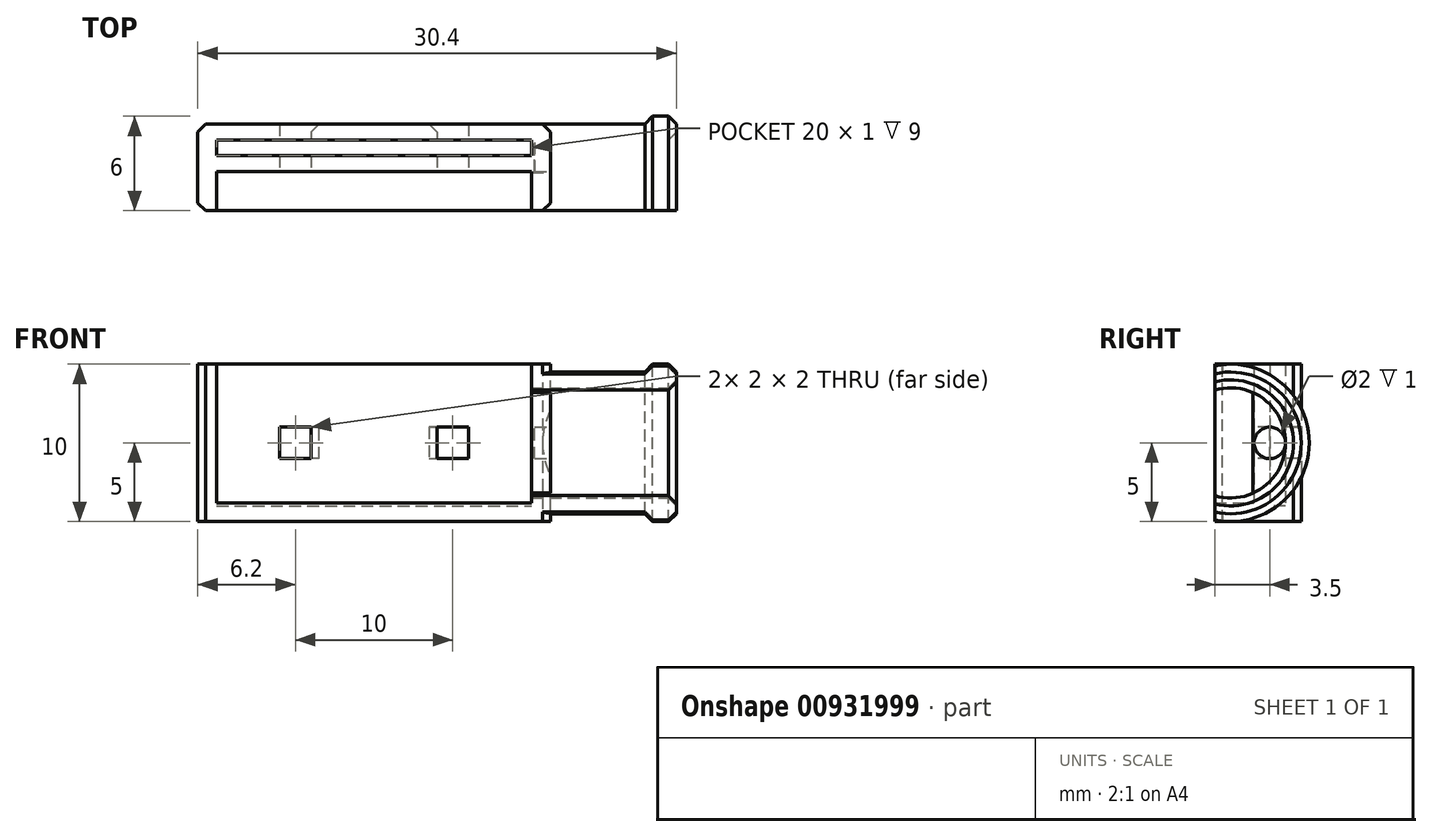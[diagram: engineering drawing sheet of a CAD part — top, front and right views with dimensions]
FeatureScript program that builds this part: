
annotation { "Feature Type Name" : "Feature", "Feature Type Description" : "" }
export const myFeature = defineFeature(function(context is Context, id is Id, definition is map)
    precondition{}
    {
        {
            var Q0;
            Q0=qCreatedBy(makeId("Top.planeOp"),FACE);
            var sketch = newSketch(context, id + "F0", { "sketchPlane" : qUnion([Q0])});
            skLineSegment(sketch, "E0.bottom", {"start": v(0, 5.5) * mm, "end": v(22.4, 5.5) * mm});
            skLineSegment(sketch, "E0.top", {"start": v(0, 0) * mm, "end": v(22.4, 0) * mm});
            skLineSegment(sketch, "E0.left", {"start": v(0, 5.5) * mm, "end": v(0, 0) * mm});
            skLineSegment(sketch, "E0.right", {"start": v(22.4, 5.5) * mm, "end": v(22.4, 0) * mm});
            skLineSegment(sketch, "E1.bottom", {"start": v(1.2, 4.5) * mm, "end": v(21.2, 4.5) * mm});
            skLineSegment(sketch, "E1.top", {"start": v(1.2, 3.5) * mm, "end": v(21.2, 3.5) * mm});
            skLineSegment(sketch, "E1.left", {"start": v(1.2, 4.5) * mm, "end": v(1.2, 3.5) * mm});
            skLineSegment(sketch, "E1.right", {"start": v(21.2, 4.5) * mm, "end": v(21.2, 3.5) * mm});
            skLineSegment(sketch, "E2.bottom", {"start": v(1.2, 0) * mm, "end": v(21.2, 0) * mm});
            skLineSegment(sketch, "E2.top", {"start": v(1.2, 2.5) * mm, "end": v(21.2, 2.5) * mm});
            skLineSegment(sketch, "E2.left", {"start": v(1.2, 0) * mm, "end": v(1.2, 2.5) * mm});
            skLineSegment(sketch, "E2.right", {"start": v(21.2, 0) * mm, "end": v(21.2, 2.5) * mm});
            skSolve(sketch);
        }
        {
            var Q0;
            Q0=makeQuery(id+"F0.imprint","IMPRINT",FACE,{"disambiguationData":[TD([[makeQuery(id+"F0.imprint","IMPRINT",EDGE,{"derivedFrom":sQuery(id+"F0.wireOp",EDGE,"E0.bottom")}),-1.0]])]});
            extrude(context, id + "F1", {"entities" : qUnion([Q0]), "depth" : 9 * mm, "offsetDistance" : 25 * mm});
        }
        {
            var Q0;
            Q0=makeQuery(id+"F1.opExtrude","CAP_FACE",FACE,{"disambiguationData":[OSD([sQuery(id+"F0.wireOp",EDGE,"E0.bottom"),sQuery(id+"F0.wireOp",EDGE,"E0.top"),sQuery(id+"F0.wireOp",EDGE,"E0.left"),sQuery(id+"F0.wireOp",EDGE,"E0.right"),sQuery(id+"F0.wireOp",EDGE,"E1.bottom"),sQuery(id+"F0.wireOp",EDGE,"E1.top"),sQuery(id+"F0.wireOp",EDGE,"E1.left"),sQuery(id+"F0.wireOp",EDGE,"E1.right")])],"isStart":true});
            var Q1;
            Q1=makeQuery(id+"F0.imprint","IMPRINT",FACE,{"disambiguationData":[TD([[makeQuery(id+"F0.imprint","IMPRINT",EDGE,{"derivedFrom":sQuery(id+"F0.wireOp",EDGE,"E1.bottom")}),-1.0]])]});
            extrude(context, id + "F2", {"entities" : qUnion([Q0, Q1]), "operationType" : NewBodyOperationType.ADD, "depth" : 1 * mm, "offsetDistance" : 25 * mm});
        }
        {
            var Q0;
            {var subQ0=sQuery(id+"F0.wireOp",EDGE,"E0.right");Q0=makeQuery(id+"F2.boolean.opBoolean","MERGE",FACE,{"derivedFrom":[makeQuery(id+"F1.opExtrude","SWEPT_FACE",FACE,{"disambiguationData":[OSD([subQ0])]}),makeQuery(id+"F2.opExtrude","SWEPT_FACE",FACE,{"disambiguationData":[OSD([subQ0])]})]});}
            var sketch = newSketch(context, id + "F3", { "sketchPlane" : qUnion([Q0])});
            skCircle(sketch, "E3", {"center": v(1, 4) * mm, "radius": 3.5 * mm});
            skCircle(sketch, "E4", {"center": v(1, 4) * mm, "radius": 4.5 * mm});
            skLineSegment(sketch, "E5", {"start": v(2.43, 7.2) * mm, "end": v(2.43, 0.8) * mm});
            skCircle(sketch, "E6", {"center": v(3.5, 4) * mm, "radius": 1 * mm});
            skSolve(sketch);
        }
        {
            var Q0;
            {var subQ0=sQuery(id+"F3.wireOp",EDGE,"E5");Q0=makeQuery(id+"F3.imprint","IMPRINT",FACE,{"disambiguationData":[TD([[makeQuery(id+"F3.imprint","IMPRINT",EDGE,{"derivedFrom":subQ0}),-1.0]])]});}
            var Q1;
            {var subQ0=sQuery(id+"F0.wireOp",EDGE,"E2.right");Q1=makeQuery(id+"F2.boolean.opBoolean","MERGE",FACE,{"derivedFrom":[makeQuery(id+"F1.opExtrude","SWEPT_FACE",FACE,{"disambiguationData":[OSD([subQ0])]}),makeQuery(id+"F2.opExtrude","SWEPT_FACE",FACE,{"disambiguationData":[OSD([subQ0])]})]});}
            extrude(context, id + "F4", {"entities" : qUnion([Q0]), "operationType" : NewBodyOperationType.REMOVE, "endBound" : BoundingType.UP_TO_SURFACE, "oppositeDirection" : true, "depth" : 25 * mm, "endBoundEntityFace" : qUnion([Q1]), "offsetDistance" : 25 * mm});
        }
        {
            var Q0;
            Q0=makeQuery(id+"F3.imprint","IMPRINT",FACE,{"disambiguationData":[TD([[makeQuery(id+"F3.imprint","IMPRINT",EDGE,{"derivedFrom":sQuery(id+"F3.wireOp",EDGE,"E6")}),1.0]])]});
            var Q1;
            {var subQ0=sQuery(id+"F0.wireOp",EDGE,"E2.right");Q1=makeQuery(id+"F2.boolean.opBoolean","MERGE",FACE,{"derivedFrom":[makeQuery(id+"F1.opExtrude","SWEPT_FACE",FACE,{"disambiguationData":[OSD([subQ0])]}),makeQuery(id+"F2.opExtrude","SWEPT_FACE",FACE,{"disambiguationData":[OSD([subQ0])]})]});}
            extrude(context, id + "F5", {"entities" : qUnion([Q0]), "operationType" : NewBodyOperationType.REMOVE, "oppositeDirection" : true, "depth" : 1 * mm, "endBoundEntityFace" : qUnion([Q1]), "offsetDistance" : 25 * mm});
        }
        {
            var Q0;
            {var subQ0=sQuery(id+"F3.wireOp",EDGE,"E5");var subQ1=sQuery(id+"F3.wireOp",EDGE,"E3");var subQ8=makeQuery(id+"F3.imprint","INTERSECT",VERTEX,{"disambiguationData":[OD(0.0)],"derivedFrom":[subQ1,subQ0]});Q0=makeQuery(id+"F3.imprint","IMPRINT",FACE,{"disambiguationData":[TD([[makeQuery(id+"F3.imprint","IMPRINT",EDGE,{"disambiguationData":[TD([[subQ8,1.0]])],"derivedFrom":subQ1}),-1.0]])]});}
            extrude(context, id + "F6", {"entities" : qUnion([Q0]), "operationType" : NewBodyOperationType.ADD, "depth" : 6 * mm, "offsetDistance" : 25 * mm});
        }
        {
            var Q0;
            {var subQ0=sQuery(id+"F0.wireOp",EDGE,"E2.top");Q0=makeQuery(id+"F2.boolean.opBoolean","MERGE",FACE,{"derivedFrom":[makeQuery(id+"F1.opExtrude","SWEPT_FACE",FACE,{"disambiguationData":[OSD([subQ0])]}),makeQuery(id+"F2.opExtrude","SWEPT_FACE",FACE,{"disambiguationData":[OSD([subQ0])]})]});}
            var sketch = newSketch(context, id + "F7", { "sketchPlane" : qUnion([Q0])});
            skLineSegment(sketch, "E7.bottom", {"start": v(5.2, 5) * mm, "end": v(7.2, 5) * mm});
            skLineSegment(sketch, "E7.top", {"start": v(5.2, 3) * mm, "end": v(7.2, 3) * mm});
            skLineSegment(sketch, "E7.left", {"start": v(5.2, 5) * mm, "end": v(5.2, 3) * mm});
            skLineSegment(sketch, "E7.right", {"start": v(7.2, 5) * mm, "end": v(7.2, 3) * mm});
            skLineSegment(sketch, "E8", {"start": v(11.2, 9) * mm, "end": v(11.2, -1) * mm, "construction": true});
            skLineSegment(sketch, "E9.MirrorCS", {"start": v(17.2, 5) * mm, "end": v(17.2, 3) * mm});
            skLineSegment(sketch, "E10.MirrorCS", {"start": v(17.2, 5) * mm, "end": v(15.2, 5) * mm});
            skLineSegment(sketch, "E11.MirrorCS", {"start": v(15.2, 5) * mm, "end": v(15.2, 3) * mm});
            skLineSegment(sketch, "E12.MirrorCS", {"start": v(17.2, 3) * mm, "end": v(15.2, 3) * mm});
            skLineSegment(sketch, "E13", {"start": v(7.2, 4) * mm, "end": v(11.2, 4) * mm, "construction": true});
            skLineSegment(sketch, "E14", {"start": v(21.2, 0.2) * mm, "end": v(1.2, 0.2) * mm});
            skSolve(sketch);
        }
        {
            var Q0;
            Q0=makeQuery(id+"F7.imprint","IMPRINT",FACE,{"disambiguationData":[TD([[makeQuery(id+"F7.imprint","IMPRINT",EDGE,{"derivedFrom":sQuery(id+"F7.wireOp",EDGE,"E7.bottom")}),-1.0]])]});
            var Q1;
            Q1=makeQuery(id+"F7.imprint","IMPRINT",FACE,{"disambiguationData":[TD([[makeQuery(id+"F7.imprint","IMPRINT",EDGE,{"derivedFrom":sQuery(id+"F7.wireOp",EDGE,"E9.MirrorCS")}),-1.0]])]});
            var Q2;
            Q2 = qConstructionFilter(qBodyType(qCreatedBy(id + "F7" ,EDGE), BodyType.WIRE), ConstructionObject.NO);
            extrude(context, id + "F8", {"entities" : qUnion([Q0, Q1]), "operationType" : NewBodyOperationType.REMOVE, "surfaceEntities" : qUnion([Q2]), "endBound" : BoundingType.THROUGH_ALL, "oppositeDirection" : true, "depth" : 25 * mm, "offsetDistance" : 25 * mm});
        }
        {
            var Q0;
            {var subQ0=sQuery(id+"F0.wireOp",EDGE,"E0.bottom");Q0=makeQuery(id+"F8.boolean.opBoolean","INTERSECT",EDGE,{"derivedFrom":[makeQuery(id+"F2.boolean.opBoolean","MERGE",FACE,{"derivedFrom":[makeQuery(id+"F1.opExtrude","SWEPT_FACE",FACE,{"disambiguationData":[OSD([subQ0])]}),makeQuery(id+"F2.opExtrude","SWEPT_FACE",FACE,{"disambiguationData":[OSD([subQ0])]})]}),makeQuery(id+"F8.opExtrude","SWEPT_FACE",FACE,{"disambiguationData":[OSD([sQuery(id+"F7.wireOp",EDGE,"E11.MirrorCS")])]})]});}
            var Q1;
            {var subQ0=sQuery(id+"F0.wireOp",EDGE,"E0.bottom");Q1=makeQuery(id+"F8.boolean.opBoolean","INTERSECT",EDGE,{"derivedFrom":[makeQuery(id+"F2.boolean.opBoolean","MERGE",FACE,{"derivedFrom":[makeQuery(id+"F1.opExtrude","SWEPT_FACE",FACE,{"disambiguationData":[OSD([subQ0])]}),makeQuery(id+"F2.opExtrude","SWEPT_FACE",FACE,{"disambiguationData":[OSD([subQ0])]})]}),makeQuery(id+"F8.opExtrude","SWEPT_FACE",FACE,{"disambiguationData":[OSD([sQuery(id+"F7.wireOp",EDGE,"E7.right")])]})]});}
            var Q2;
            Q2=makeQuery(id+"F8.boolean.opBoolean","COPY",EDGE,{"derivedFrom":makeQuery(id+"F8.opExtrude","CAP_EDGE",EDGE,{"disambiguationData":[OSD([sQuery(id+"F7.wireOp",EDGE,"E7.right")])],"isStart":true})});
            var Q3;
            Q3=makeQuery(id+"F8.boolean.opBoolean","COPY",EDGE,{"derivedFrom":makeQuery(id+"F8.opExtrude","CAP_EDGE",EDGE,{"disambiguationData":[OSD([sQuery(id+"F7.wireOp",EDGE,"E11.MirrorCS")])],"isStart":true})});
            var Q4;
            {var subQ0=sQuery(id+"F0.wireOp",EDGE,"E0.left");var subQ1=sQuery(id+"F0.wireOp",EDGE,"E0.bottom");Q4=makeQuery(id+"F2.boolean.opBoolean","MERGE",EDGE,{"derivedFrom":[makeQuery(id+"F1.opExtrude","SWEPT_EDGE",EDGE,{"disambiguationData":[OSD([subQ1,subQ0])]}),makeQuery(id+"F2.opExtrude","SWEPT_EDGE",EDGE,{"disambiguationData":[OSD([subQ1,subQ0])]})]});}
            var Q5;
            {var subQ0=sQuery(id+"F0.wireOp",EDGE,"E0.right");var subQ1=sQuery(id+"F0.wireOp",EDGE,"E0.bottom");Q5=makeQuery(id+"F6.boolean.opBoolean","SPLIT",EDGE,{"disambiguationData":[TD([makeQuery(id+"F1.opExtrude","CAP_FACE",FACE,{"disambiguationData":[OSD([subQ1,sQuery(id+"F0.wireOp",EDGE,"E0.top"),sQuery(id+"F0.wireOp",EDGE,"E0.left"),subQ0,sQuery(id+"F0.wireOp",EDGE,"E1.bottom"),sQuery(id+"F0.wireOp",EDGE,"E1.top"),sQuery(id+"F0.wireOp",EDGE,"E1.left"),sQuery(id+"F0.wireOp",EDGE,"E1.right"),sQuery(id+"F0.wireOp",EDGE,"E2.top"),sQuery(id+"F0.wireOp",EDGE,"E2.left"),sQuery(id+"F0.wireOp",EDGE,"E2.right")])],"isStart":false})])],"derivedFrom":makeQuery(id+"F2.boolean.opBoolean","MERGE",EDGE,{"derivedFrom":[makeQuery(id+"F1.opExtrude","SWEPT_EDGE",EDGE,{"disambiguationData":[OSD([subQ1,subQ0])]}),makeQuery(id+"F2.opExtrude","SWEPT_EDGE",EDGE,{"disambiguationData":[OSD([subQ1,subQ0])]})]})});}
            var Q6;
            {var subQ0=sQuery(id+"F0.wireOp",EDGE,"E0.left");var subQ1=sQuery(id+"F0.wireOp",EDGE,"E0.top");Q6=makeQuery(id+"F2.boolean.opBoolean","MERGE",EDGE,{"derivedFrom":[makeQuery(id+"F1.opExtrude","SWEPT_EDGE",EDGE,{"disambiguationData":[OSD([subQ1,subQ0])]}),makeQuery(id+"F2.opExtrude","SWEPT_EDGE",EDGE,{"disambiguationData":[OSD([subQ1,subQ0])]})]});}
            var Q7;
            {var subQ0=sQuery(id+"F0.wireOp",EDGE,"E0.right");var subQ1=sQuery(id+"F0.wireOp",EDGE,"E0.top");var subQ4=sQuery(id+"F3.wireOp",EDGE,"E3");var subQ5=makeQuery(id+"F2.boolean.opBoolean","MERGE",EDGE,{"derivedFrom":[makeQuery(id+"F1.opExtrude","SWEPT_EDGE",EDGE,{"disambiguationData":[OSD([subQ1,subQ0])]}),makeQuery(id+"F2.opExtrude","SWEPT_EDGE",EDGE,{"disambiguationData":[OSD([subQ1,subQ0])]})]});Q7=makeQuery(id+"F4.boolean.opBoolean","SPLIT",EDGE,{"disambiguationData":[TD([makeQuery(id+"F4.opExtrude","SWEPT_FACE",FACE,{"disambiguationData":[OSD([subQ4]),TDD([makeQuery(id+"F3.imprint","IMPRINT",EDGE,{"disambiguationData":[TD([[makeQuery(id+"F3.imprint","INTERSECT",VERTEX,{"disambiguationData":[OD(0.0)],"derivedFrom":[subQ4,sQuery(id+"F3.wireOp",EDGE,"E5")]}),-1.0]])],"derivedFrom":subQ4})])]})])],"derivedFrom":subQ5});}
            var Q8;
            {var subQ4=sQuery(id+"F0.wireOp",EDGE,"E0.right");var subQ5=sQuery(id+"F0.wireOp",EDGE,"E0.top");var subQ8=sQuery(id+"F3.wireOp",EDGE,"E3");var subQ9=makeQuery(id+"F2.boolean.opBoolean","MERGE",EDGE,{"derivedFrom":[makeQuery(id+"F1.opExtrude","SWEPT_EDGE",EDGE,{"disambiguationData":[OSD([subQ5,subQ4])]}),makeQuery(id+"F2.opExtrude","SWEPT_EDGE",EDGE,{"disambiguationData":[OSD([subQ5,subQ4])]})]});Q8=makeQuery(id+"F4.boolean.opBoolean","SPLIT",EDGE,{"disambiguationData":[TD([makeQuery(id+"F4.opExtrude","SWEPT_FACE",FACE,{"disambiguationData":[OSD([subQ8]),TDD([makeQuery(id+"F3.imprint","IMPRINT",EDGE,{"disambiguationData":[TD([[makeQuery(id+"F3.imprint","INTERSECT",VERTEX,{"disambiguationData":[OD(1.0)],"derivedFrom":[subQ8,sQuery(id+"F3.wireOp",EDGE,"E5")]}),1.0]])],"derivedFrom":subQ8})])]})])],"derivedFrom":subQ9});}
            chamfer(context, id + "F9", {"entities" : qUnion([Q0, Q1, Q2, Q3, Q4, Q5, Q6, Q7, Q8]), "width" : 0.5 * mm, "tangentPropagation" : true});
        }
        {
            var Q0;
            Q0=makeQuery(id+"F6.opExtrude","CAP_FACE",FACE,{"disambiguationData":[OSD([sQuery(id+"F0.wireOp",EDGE,"E0.top"),sQuery(id+"F0.wireOp",EDGE,"E0.right"),sQuery(id+"F3.wireOp",EDGE,"E3"),sQuery(id+"F3.wireOp",EDGE,"E4")])],"isStart":false});
            var sketch = newSketch(context, id + "F10", { "sketchPlane" : qUnion([Q0])});
            skArc(sketch, "E15", {"start": v(0, -0.9) * mm, "mid": v(6, 4) * mm, "end": v(0, 8.9) * mm});
            skLineSegment(sketch, "E16", {"start": v(0, -0.39) * mm, "end": v(0, -0.9) * mm});
            skLineSegment(sketch, "E17", {"start": v(0, 8.39) * mm, "end": v(0, 8.9) * mm});
            skSolve(sketch);
        }
        {
            var Q0;
            Q0=makeQuery(id+"F10.imprint","IMPRINT",FACE,{"disambiguationData":[TD([[makeQuery(id+"F10.imprint","IMPRINT",EDGE,{"derivedFrom":sQuery(id+"F10.wireOp",EDGE,"E15")}),1.0]])]});
            var Q1;
            {var subQ0=sQuery(id+"F3.wireOp",EDGE,"E3");Q1=makeQuery(id+"F10.imprint","IMPRINT",FACE,{"disambiguationData":[TD([[makeQuery(id+"F10.imprint","IMPRINT",EDGE,{"derivedFrom":makeQuery(id+"F6.opExtrude","CAP_EDGE",EDGE,{"disambiguationData":[OSD([subQ0])],"isStart":false})}),-1.0]])]});}
            extrude(context, id + "F11", {"entities" : qUnion([Q0, Q1]), "operationType" : NewBodyOperationType.ADD, "depth" : 2 * mm, "offsetDistance" : 25 * mm});
        }
        {
            var Q0;
            Q0=makeQuery(id+"F11.opExtrude","CAP_EDGE",EDGE,{"disambiguationData":[OSD([sQuery(id+"F10.wireOp",EDGE,"E15")])],"isStart":true});
            var Q1;
            Q1=makeQuery(id+"F11.opExtrude","CAP_EDGE",EDGE,{"disambiguationData":[OSD([sQuery(id+"F10.wireOp",EDGE,"E15")])],"isStart":false});
            var Q2;
            Q2=makeQuery(id+"F11.opExtrude","CAP_EDGE",EDGE,{"disambiguationData":[OSD([sQuery(id+"F3.wireOp",EDGE,"E3")])],"isStart":false});
            chamfer(context, id + "F12", {"entities" : qUnion([Q0, Q1, Q2]), "width" : 0.5 * mm, "tangentPropagation" : true});
        }
        {
            var Q0;
            {var subQ0=sQuery(id+"F7.wireOp",EDGE,"E14");Q0=makeQuery(id+"F7.imprint","IMPRINT",FACE,{"disambiguationData":[TD([[makeQuery(id+"F7.imprint","IMPRINT",EDGE,{"derivedFrom":subQ0}),1.0]])]});}
            var Q1;
            {var subQ0=sQuery(id+"F0.wireOp",EDGE,"E0.top");var subQ1=makeQuery(id+"F0.imprint","IMPRINT",EDGE,{"disambiguationData":[TD([[makeQuery(id+"F0.imprint","INTERSECT",VERTEX,{"derivedFrom":[subQ0,sQuery(id+"F0.wireOp",EDGE,"E0.left")]}),-1.0]])],"derivedFrom":subQ0});Q1=makeQuery(id+"F2.boolean.opBoolean","MERGE",FACE,{"derivedFrom":[makeQuery(id+"F1.opExtrude","SWEPT_FACE",FACE,{"disambiguationData":[OSD([subQ0]),TDD([subQ1])]}),makeQuery(id+"F2.opExtrude","SWEPT_FACE",FACE,{"disambiguationData":[OSD([subQ0]),TDD([makeQuery(id+"F1.opExtrude","CAP_EDGE",EDGE,{"disambiguationData":[OSD([subQ0]),TDD([subQ1])],"isStart":true})])]})]});}
            extrude(context, id + "F13", {"entities" : qUnion([Q0]), "operationType" : NewBodyOperationType.ADD, "endBound" : BoundingType.UP_TO_SURFACE, "depth" : 25 * mm, "endBoundEntityFace" : qUnion([Q1]), "offsetDistance" : 25 * mm});
        }
    });
